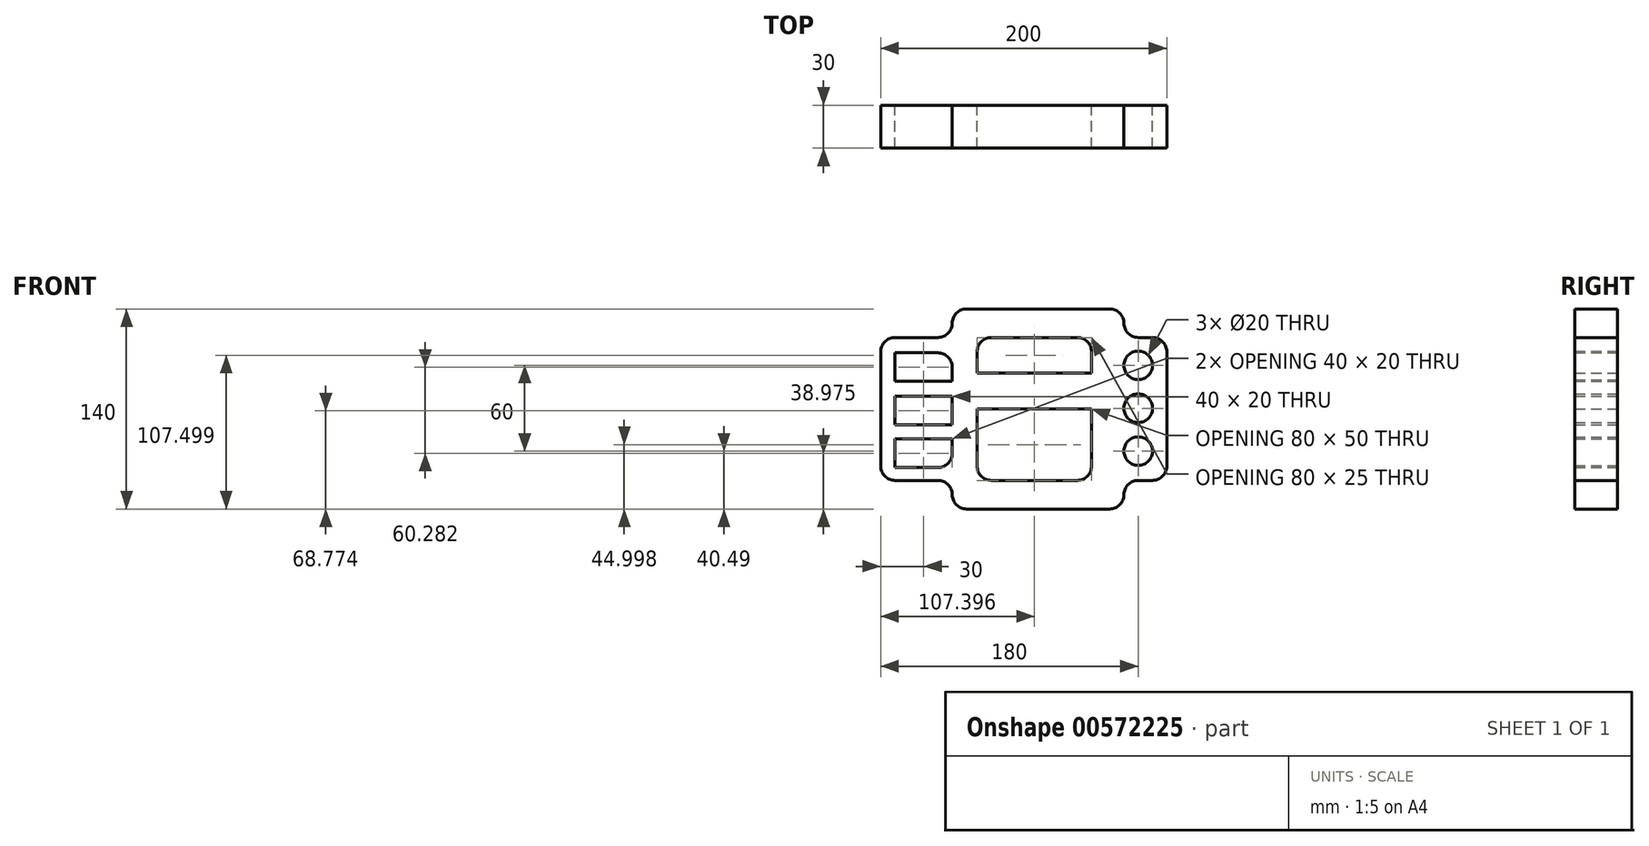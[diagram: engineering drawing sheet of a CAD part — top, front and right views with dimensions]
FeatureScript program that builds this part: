
annotation { "Feature Type Name" : "Feature", "Feature Type Description" : "" }
export const myFeature = defineFeature(function(context is Context, id is Id, definition is map)
    precondition{}
    {
        {
            var Q0;
            Q0=qCreatedBy(makeId("Front.planeOp"),FACE);
            var sketch = newSketch(context, id + "F0", { "sketchPlane" : qUnion([Q0])});
            skLineSegment(sketch, "E0.bottom", {"start": v(-10.3, -40.5) * mm, "end": v(89.7, -40.5) * mm});
            skLineSegment(sketch, "E0.top", {"start": v(-10.3, 99.5) * mm, "end": v(89.7, 99.5) * mm});
            skLineSegment(sketch, "E0.left", {"start": v(-20.3, -30.5) * mm, "end": v(-20.3, -30.5) * mm});
            skLineSegment(sketch, "E0.right", {"start": v(99.7, -30.5) * mm, "end": v(99.7, -30.5) * mm});
            skLineSegment(sketch, "E1.bottom", {"start": v(-60.3, 79.5) * mm, "end": v(-30.3, 79.5) * mm});
            skLineSegment(sketch, "E1.top", {"start": v(-60.3, -20.5) * mm, "end": v(-30.3, -20.5) * mm});
            skLineSegment(sketch, "E1.left", {"start": v(-70.3, 69.5) * mm, "end": v(-70.3, -10.5) * mm});
            skLineSegment(sketch, "E1.right", {"start": v(129.7, 69.5) * mm, "end": v(129.7, -10.5) * mm});
            skLineSegment(sketch, "E2.trimOffspring", {"start": v(-20.3, 89.5) * mm, "end": v(-20.3, 89.5) * mm});
            skLineSegment(sketch, "E3.trimOffspring", {"start": v(99.7, 89.5) * mm, "end": v(99.7, 89.5) * mm});
            skLineSegment(sketch, "E4.trimOffspring", {"start": v(109.7, 79.5) * mm, "end": v(119.7, 79.5) * mm});
            skLineSegment(sketch, "E5.trimOffspring", {"start": v(109.7, -20.5) * mm, "end": v(119.7, -20.5) * mm});
            skLineSegment(sketch, "E6.bottom", {"start": v(7.1, 79.5) * mm, "end": v(67.1, 79.5) * mm});
            skLineSegment(sketch, "E6.top", {"start": v(7.1, -20.5) * mm, "end": v(67.1, -20.5) * mm});
            skLineSegment(sketch, "E6.left", {"start": v(-2.9, 69.5) * mm, "end": v(-2.9, 54.5) * mm});
            skLineSegment(sketch, "E6.right", {"start": v(77.1, 69.5) * mm, "end": v(77.1, 54.5) * mm});
            skLineSegment(sketch, "E7.bottom", {"start": v(-2.9, 54.5) * mm, "end": v(77.1, 54.5) * mm});
            skLineSegment(sketch, "E7.top", {"start": v(-2.9, 29.5) * mm, "end": v(77.1, 29.5) * mm});
            skLineSegment(sketch, "E8.trimOffspring", {"start": v(-2.9, 29.5) * mm, "end": v(-2.9, -10.5) * mm});
            skLineSegment(sketch, "E9.trimOffspring", {"start": v(77.1, 29.5) * mm, "end": v(77.1, -10.5) * mm});
            skCircle(sketch, "E10", {"center": v(109.7, 60) * mm, "radius": 10 * mm});
            skCircle(sketch, "E11", {"center": v(109.7, 30) * mm, "radius": 10 * mm});
            skCircle(sketch, "E12", {"center": v(109.7, 0) * mm, "radius": 10 * mm});
            skLineSegment(sketch, "E13.bottom", {"start": v(-60.3, 68.77) * mm, "end": v(-30.3, 68.77) * mm});
            skLineSegment(sketch, "E13.top", {"start": v(-60.3, 48.77) * mm, "end": v(-20.3, 48.77) * mm});
            skLineSegment(sketch, "E13.left", {"start": v(-60.3, 68.77) * mm, "end": v(-60.3, 48.77) * mm});
            skLineSegment(sketch, "E13.right", {"start": v(-20.3, 58.77) * mm, "end": v(-20.3, 48.77) * mm});
            skLineSegment(sketch, "E14.bottom", {"start": v(-60.3, 38.28) * mm, "end": v(-20.3, 38.28) * mm});
            skLineSegment(sketch, "E14.top", {"start": v(-60.3, 18.28) * mm, "end": v(-20.3, 18.28) * mm});
            skLineSegment(sketch, "E14.left", {"start": v(-60.3, 38.28) * mm, "end": v(-60.3, 18.28) * mm});
            skLineSegment(sketch, "E14.right", {"start": v(-20.3, 38.28) * mm, "end": v(-20.3, 18.28) * mm});
            skLineSegment(sketch, "E15.bottom", {"start": v(-60.3, 8.49) * mm, "end": v(-20.3, 8.49) * mm});
            skLineSegment(sketch, "E15.top", {"start": v(-60.3, -11.51) * mm, "end": v(-30.3, -11.51) * mm});
            skLineSegment(sketch, "E15.left", {"start": v(-60.3, 8.49) * mm, "end": v(-60.3, -11.51) * mm});
            skLineSegment(sketch, "E15.right", {"start": v(-20.3, 8.49) * mm, "end": v(-20.3, -1.51) * mm});
            skPoint(sketch, "E16.visualSharp", {"position": v(-70.3, 79.5) * mm});
            skArc(sketch, "E16.filletArc", {"start": v(-60.3, 79.5) * mm, "mid": v(-67.37, 76.58) * mm, "end": v(-70.3, 69.5) * mm});
            skPoint(sketch, "E17.visualSharp", {"position": v(-20.3, 79.5) * mm});
            skArc(sketch, "E17.filletArc", {"start": v(-30.3, 79.5) * mm, "mid": v(-23.23, 82.44) * mm, "end": v(-20.3, 89.5) * mm});
            skPoint(sketch, "E18.visualSharp", {"position": v(-20.3, 99.5) * mm});
            skArc(sketch, "E18.filletArc", {"start": v(-10.3, 99.5) * mm, "mid": v(-17.37, 96.58) * mm, "end": v(-20.3, 89.5) * mm});
            skPoint(sketch, "E19.visualSharp", {"position": v(99.7, 99.5) * mm});
            skArc(sketch, "E19.filletArc", {"start": v(99.7, 89.5) * mm, "mid": v(96.77, 96.58) * mm, "end": v(89.7, 99.5) * mm});
            skPoint(sketch, "E20.visualSharp", {"position": v(99.7, 79.5) * mm});
            skArc(sketch, "E20.filletArc", {"start": v(99.7, 89.5) * mm, "mid": v(102.63, 82.44) * mm, "end": v(109.7, 79.5) * mm});
            skPoint(sketch, "E21.visualSharp", {"position": v(129.7, 79.5) * mm});
            skArc(sketch, "E21.filletArc", {"start": v(129.7, 69.5) * mm, "mid": v(126.77, 76.58) * mm, "end": v(119.7, 79.5) * mm});
            skPoint(sketch, "E22.visualSharp", {"position": v(129.7, -20.5) * mm});
            skArc(sketch, "E22.filletArc", {"start": v(119.7, -20.5) * mm, "mid": v(126.77, -17.56) * mm, "end": v(129.7, -10.5) * mm});
            skPoint(sketch, "E23.visualSharp", {"position": v(99.7, -20.5) * mm});
            skArc(sketch, "E23.filletArc", {"start": v(109.7, -20.5) * mm, "mid": v(102.63, -23.42) * mm, "end": v(99.7, -30.5) * mm});
            skPoint(sketch, "E24.visualSharp", {"position": v(99.7, -40.5) * mm});
            skArc(sketch, "E24.filletArc", {"start": v(89.7, -40.5) * mm, "mid": v(96.77, -37.56) * mm, "end": v(99.7, -30.5) * mm});
            skPoint(sketch, "E25.visualSharp", {"position": v(-20.3, -40.5) * mm});
            skArc(sketch, "E25.filletArc", {"start": v(-20.3, -30.5) * mm, "mid": v(-17.37, -37.56) * mm, "end": v(-10.3, -40.5) * mm});
            skPoint(sketch, "E26.visualSharp", {"position": v(-20.3, -20.5) * mm});
            skArc(sketch, "E26.filletArc", {"start": v(-20.3, -30.5) * mm, "mid": v(-23.23, -23.42) * mm, "end": v(-30.3, -20.5) * mm});
            skPoint(sketch, "E27.visualSharp", {"position": v(-70.3, -20.5) * mm});
            skArc(sketch, "E27.filletArc", {"start": v(-70.3, -10.5) * mm, "mid": v(-67.37, -17.56) * mm, "end": v(-60.3, -20.5) * mm});
            skPoint(sketch, "E28.visualSharp", {"position": v(-20.3, 68.77) * mm});
            skArc(sketch, "E28.filletArc", {"start": v(-20.3, 58.77) * mm, "mid": v(-23.23, 65.84) * mm, "end": v(-30.3, 68.77) * mm});
            skPoint(sketch, "E29.visualSharp", {"position": v(-20.3, -11.51) * mm});
            skArc(sketch, "E29.filletArc", {"start": v(-30.3, -11.51) * mm, "mid": v(-23.23, -8.59) * mm, "end": v(-20.3, -1.51) * mm});
            skPoint(sketch, "E30.visualSharp", {"position": v(77.1, 79.5) * mm});
            skArc(sketch, "E30.filletArc", {"start": v(77.1, 69.5) * mm, "mid": v(74.17, 76.58) * mm, "end": v(67.1, 79.5) * mm});
            skPoint(sketch, "E31.visualSharp", {"position": v(-2.9, 79.5) * mm});
            skArc(sketch, "E31.filletArc", {"start": v(7.1, 79.5) * mm, "mid": v(0.03, 76.58) * mm, "end": v(-2.9, 69.5) * mm});
            skPoint(sketch, "E32.visualSharp", {"position": v(-2.9, -20.5) * mm});
            skArc(sketch, "E32.filletArc", {"start": v(-2.9, -10.5) * mm, "mid": v(0.03, -17.56) * mm, "end": v(7.1, -20.5) * mm});
            skPoint(sketch, "E33.visualSharp", {"position": v(77.1, -20.5) * mm});
            skArc(sketch, "E33.filletArc", {"start": v(67.1, -20.5) * mm, "mid": v(74.17, -17.56) * mm, "end": v(77.1, -10.5) * mm});
            skSolve(sketch);
        }
        {
            var Q0;
            Q0 = qSketchRegion(id + "F0", true);
            extrude(context, id + "F1", {"entities" : qUnion([Q0]), "depth" : 30 * mm, "offsetDistance" : 25 * mm});
        }
        {
            var Q0;
            Q0 = qSketchRegion(id + "F0", true);
            extrude(context, id + "F2", {"entities" : qUnion([Q0]), "operationType" : NewBodyOperationType.ADD, "depth" : 30 * mm, "offsetDistance" : 25 * mm});
        }
    });
